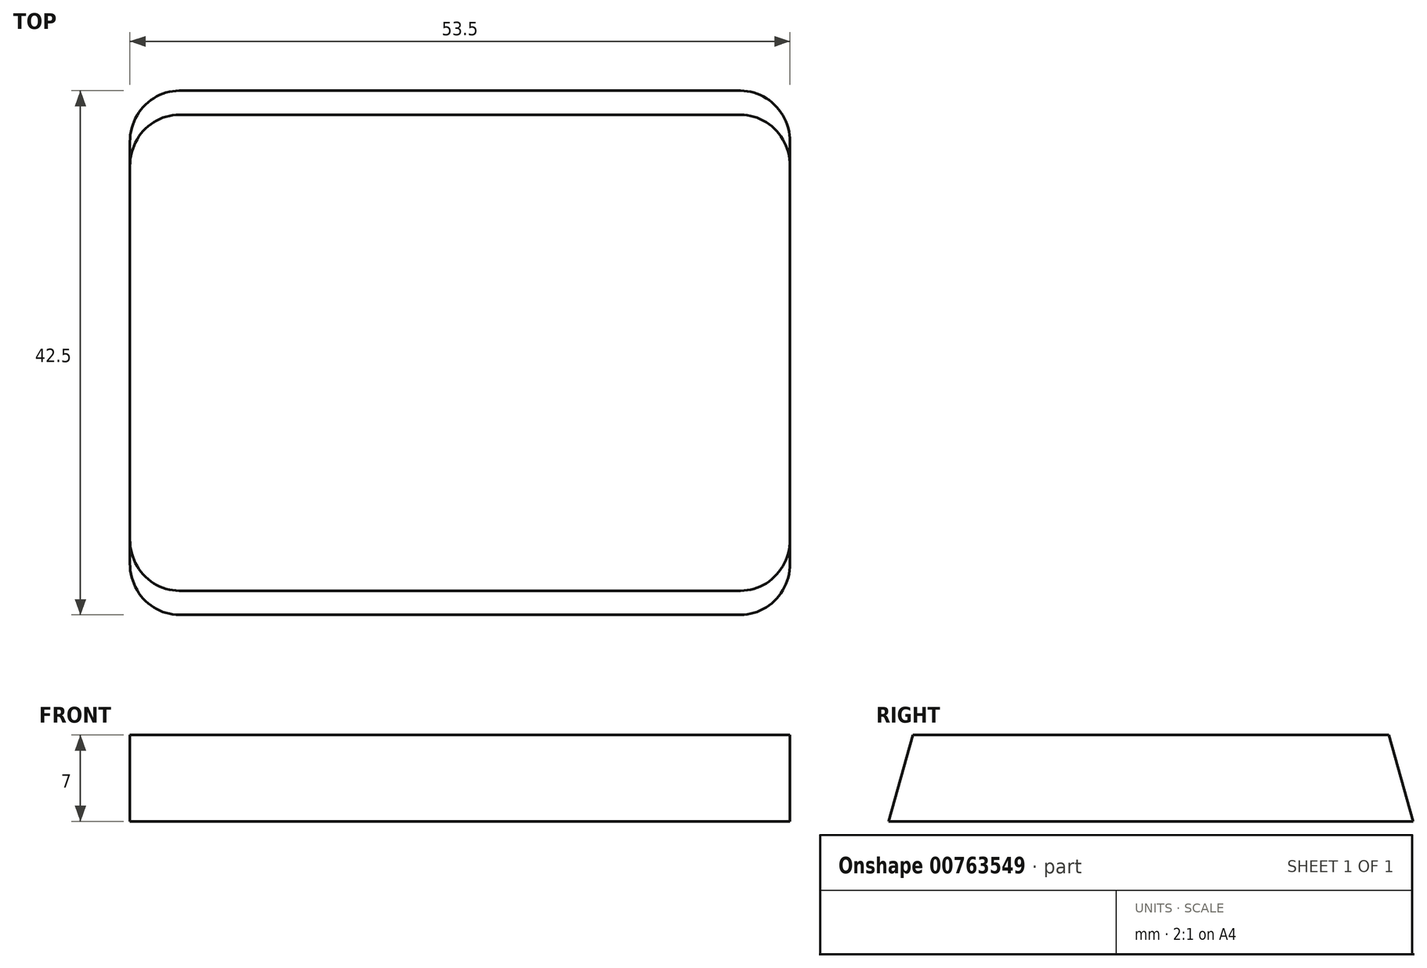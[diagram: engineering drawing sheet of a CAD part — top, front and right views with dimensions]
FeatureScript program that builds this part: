
annotation { "Feature Type Name" : "Feature", "Feature Type Description" : "" }
export const myFeature = defineFeature(function(context is Context, id is Id, definition is map)
    precondition{}
    {
        {
            assignVariable(context, id + "F0", {"name" : "base_width", "anyValue" : 53.5});
        }
        {
            var Q0;
            Q0=qCreatedBy(makeId("Right.planeOp"),FACE);
            var sketch = newSketch(context, id + "F1", { "sketchPlane" : qUnion([Q0])});
            skLineSegment(sketch, "E0", {"start": v(-21.25, 0) * mm, "end": v(21.25, 0) * mm});
            skLineSegment(sketch, "E1", {"start": v(21.25, 0) * mm, "end": v(19.3, 7) * mm});
            skLineSegment(sketch, "E2", {"start": v(19.3, 7) * mm, "end": v(-19.3, 7) * mm});
            skLineSegment(sketch, "E3", {"start": v(-19.3, 7) * mm, "end": v(-21.25, 0) * mm});
            skLineSegment(sketch, "E4", {"start": v(0, 0) * mm, "end": v(0, 7) * mm, "construction": true});
            skSolve(sketch);
        }
        {
            var Q0;
            Q0=makeQuery(id+"F1.imprint","IMPRINT",FACE,{"disambiguationData":[TD([[makeQuery(id+"F1.imprint","IMPRINT",EDGE,{"derivedFrom":sQuery(id+"F1.wireOp",EDGE,"E0")}),1.0]])]});
            extrude(context, id + "F2", {"entities" : qUnion([Q0]), "depth" : (getVariable(context, 'base_width')) * mm, "symmetric" : true});
        }
        {
            var Q0;
            Q0=makeQuery(id+"F2.opExtrude","CAP_EDGE",EDGE,{"disambiguationData":[OSD([sQuery(id+"F1.wireOp",EDGE,"E3")])],"isStart":true});
            var Q1;
            Q1=makeQuery(id+"F2.opExtrude","CAP_EDGE",EDGE,{"disambiguationData":[OSD([sQuery(id+"F1.wireOp",EDGE,"E3")])],"isStart":false});
            var Q2;
            Q2=makeQuery(id+"F2.opExtrude","CAP_EDGE",EDGE,{"disambiguationData":[OSD([sQuery(id+"F1.wireOp",EDGE,"E1")])],"isStart":false});
            var Q3;
            Q3=makeQuery(id+"F2.opExtrude","CAP_EDGE",EDGE,{"disambiguationData":[OSD([sQuery(id+"F1.wireOp",EDGE,"E1")])],"isStart":true});
            fillet(context, id + "F3", {"entities" : qUnion([Q0, Q1, Q2, Q3]), "radius" : 4 * mm, "tangentPropagation" : true, "allowEdgeOverflow" : false});
        }
    });
